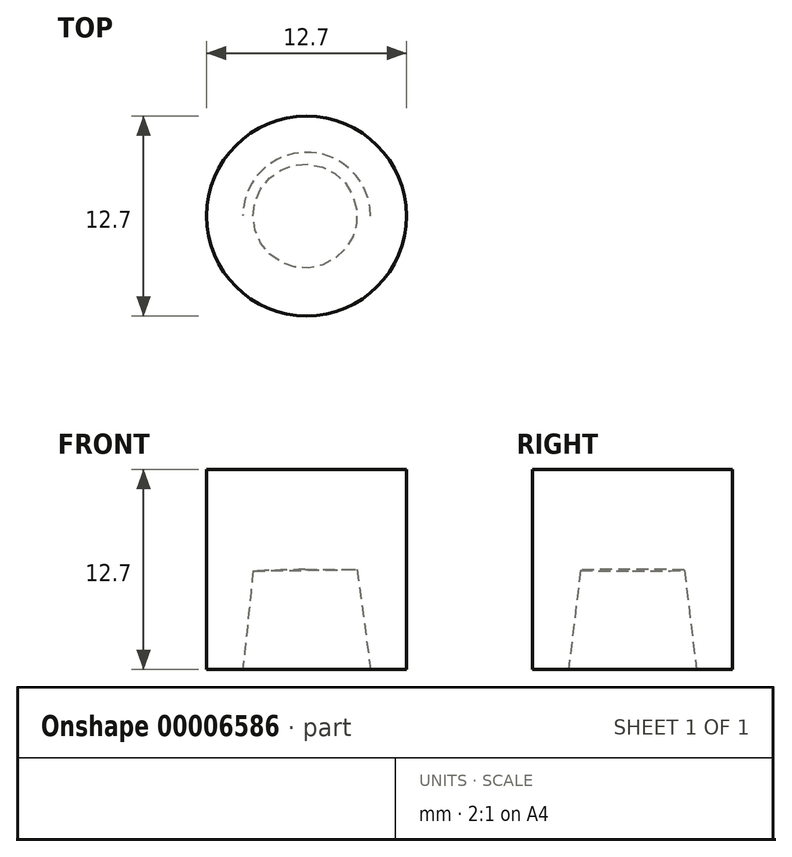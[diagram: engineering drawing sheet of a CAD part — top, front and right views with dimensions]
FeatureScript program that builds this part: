
annotation { "Feature Type Name" : "Feature", "Feature Type Description" : "" }
export const myFeature = defineFeature(function(context is Context, id is Id, definition is map)
    precondition{}
    {
        {
            var Q0;
            Q0=qCreatedBy(makeId("Front.planeOp"),FACE);
            var sketch = newSketch(context, id + "F0", { "sketchPlane" : qUnion([Q0])});
            skLineSegment(sketch, "E0", {"start": v(-0.09, 6.35) * mm, "end": v(3.21, 6.35) * mm});
            skLineSegment(sketch, "E1", {"start": v(3.21, 6.35) * mm, "end": v(4.06, 0) * mm});
            skLineSegment(sketch, "E2", {"start": v(4.06, 0) * mm, "end": v(0, 0) * mm});
            skLineSegment(sketch, "E3", {"start": v(0, 0) * mm, "end": v(-0.09, 6.35) * mm});
            skSolve(sketch);
        }
        {
            var Q0;
            Q0=qCreatedBy(makeId("Top.planeOp"),FACE);
            var sketch = newSketch(context, id + "F1", { "sketchPlane" : qUnion([Q0])});
            skCircle(sketch, "E4", {"center": v(0, 0) * mm, "radius": 6.35 * mm});
            skSolve(sketch);
        }
        {
            var Q0;
            Q0 = qSketchRegion(id + "F1", true);
            extrude(context, id + "F2", {"entities" : qUnion([Q0]), "depth" : 12.7 * mm});
        }
        {
            var Q0;
            Q0=makeQuery(id+"F0.imprint","IMPRINT",FACE,{"disambiguationData":[TD([[makeQuery(id+"F0.imprint","IMPRINT",EDGE,{"derivedFrom":sQuery(id+"F0.wireOp",EDGE,"E0")}),-1.0]])]});
            var Q1;
            Q1=sQuery(id+"F0.wireOp",EDGE,"E3");
            revolve(context, id + "F3", {"operationType" : NewBodyOperationType.REMOVE, "entities" : qUnion([Q0]), "axis" : qUnion([Q1]), "revolveType" : RevolveType.FULL});
        }
    });
